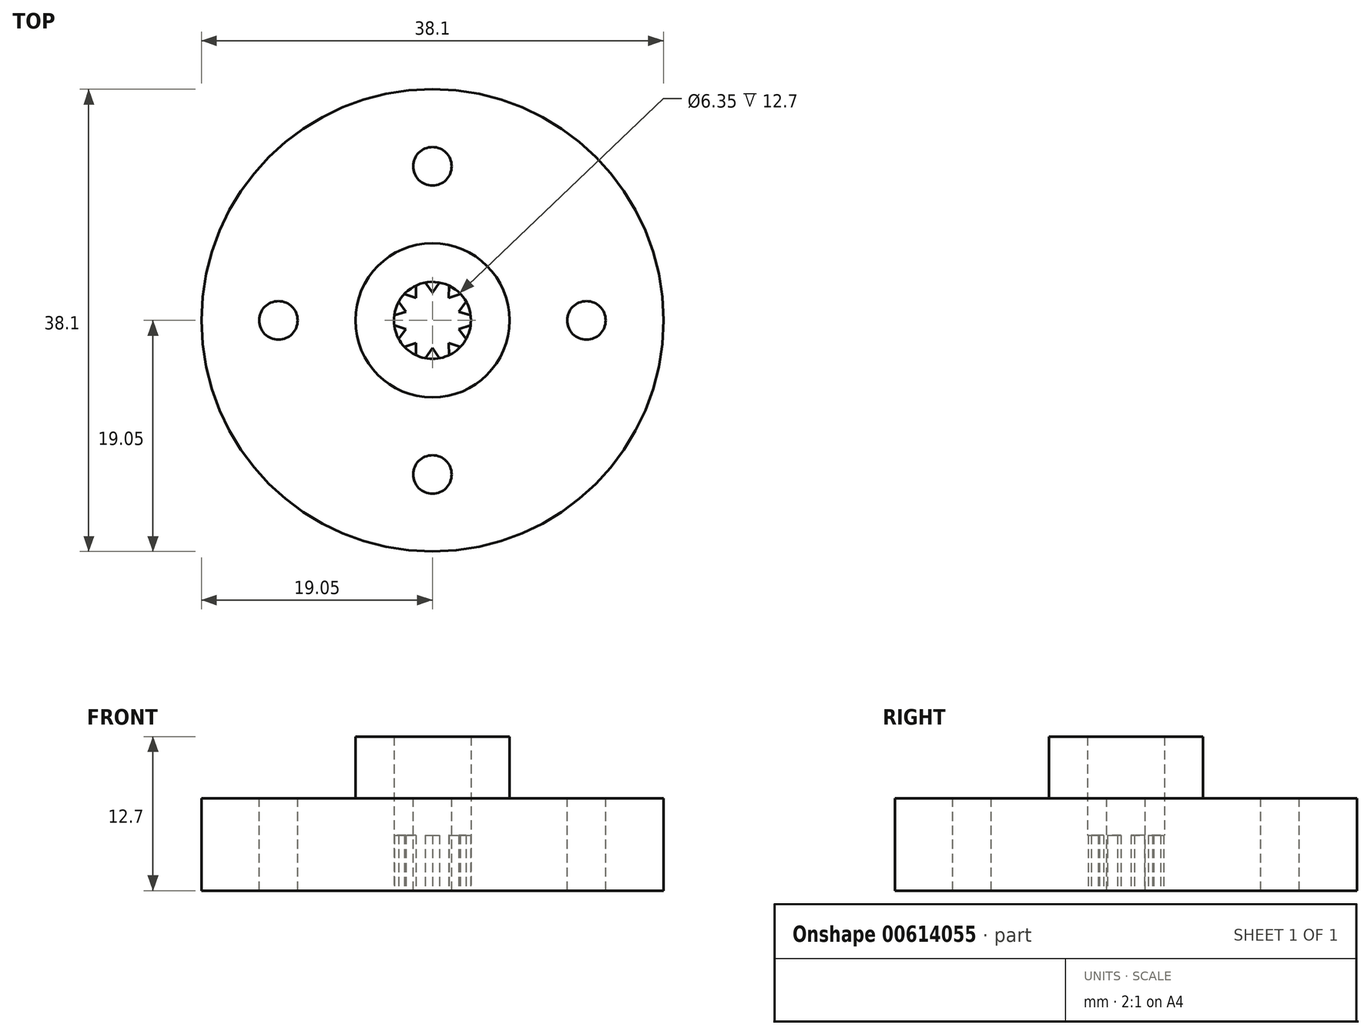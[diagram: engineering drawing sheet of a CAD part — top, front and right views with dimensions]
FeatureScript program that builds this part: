
annotation { "Feature Type Name" : "Feature", "Feature Type Description" : "" }
export const myFeature = defineFeature(function(context is Context, id is Id, definition is map)
    precondition{}
    {
        {
            var Q0;
            Q0=qCreatedBy(makeId("Top.planeOp"),FACE);
            var sketch = newSketch(context, id + "F0", { "sketchPlane" : qUnion([Q0])});
            skCircle(sketch, "E0", {"center": v(0, 0) * mm, "radius": 3.18 * mm});
            skCircle(sketch, "E1", {"center": v(0, 0) * mm, "radius": 6.35 * mm});
            skSolve(sketch);
        }
        {
            var Q0;
            Q0 = qSketchRegion(id + "F0", true);
            extrude(context, id + "F1", {"entities" : qUnion([Q0]), "depth" : 12.7 * mm, "offsetDistance" : 25.4 * mm});
        }
        {
            var Q0;
            Q0=qCreatedBy(makeId("Top.planeOp"),FACE);
            var sketch = newSketch(context, id + "F2", { "sketchPlane" : qUnion([Q0])});
            skCircle(sketch, "E2", {"center": v(0, 0) * mm, "radius": 6.35 * mm});
            skCircle(sketch, "E3", {"center": v(0, 0) * mm, "radius": 19.05 * mm});
            skSolve(sketch);
        }
        {
            var Q0;
            Q0 = qSketchRegion(id + "F2", true);
            extrude(context, id + "F3", {"entities" : qUnion([Q0]), "operationType" : NewBodyOperationType.ADD, "depth" : 7.62 * mm, "offsetDistance" : 25.4 * mm});
        }
        {
            var Q0;
            Q0=qCreatedBy(makeId("Top.planeOp"),FACE);
            var sketch = newSketch(context, id + "F4", { "sketchPlane" : qUnion([Q0])});
            skPoint(sketch, "E4.0.midPoint", {"position": v(0, 2.29) * mm});
            skLineSegment(sketch, "E5", {"start": v(0, 2.29) * mm, "end": v(0, 3.43) * mm});
            skLineSegment(sketch, "E6", {"start": v(0, 3.43) * mm, "end": v(-0.8, 3.43) * mm});
            skLineSegment(sketch, "E7", {"start": v(-0.8, 3.43) * mm, "end": v(0, 2.29) * mm});
            skLineSegment(sketch, "E8", {"start": v(0, 2.29) * mm, "end": v(0.8, 3.43) * mm});
            skLineSegment(sketch, "E9", {"start": v(0.8, 3.43) * mm, "end": v(0, 3.43) * mm});
            skLineSegment(sketch, "E10", {"start": v(1.34, 1.85) * mm, "end": v(2.02, 2.77) * mm});
            skLineSegment(sketch, "E11", {"start": v(2.02, 2.77) * mm, "end": v(1.37, 3.25) * mm});
            skLineSegment(sketch, "E12", {"start": v(1.37, 3.25) * mm, "end": v(1.34, 1.85) * mm});
            skLineSegment(sketch, "E13", {"start": v(1.34, 1.85) * mm, "end": v(2.67, 2.3) * mm});
            skLineSegment(sketch, "E14", {"start": v(2.67, 2.3) * mm, "end": v(2.02, 2.77) * mm});
            skLineSegment(sketch, "E15.0", {"start": v(2.02, 2.77) * mm, "end": v(2.67, 2.3) * mm, "construction": true});
            skLineSegment(sketch, "E16", {"start": v(2.17, 0.7) * mm, "end": v(3.26, 1.06) * mm});
            skLineSegment(sketch, "E17", {"start": v(3.26, 1.06) * mm, "end": v(3.01, 1.82) * mm});
            skLineSegment(sketch, "E18", {"start": v(3.01, 1.82) * mm, "end": v(2.17, 0.7) * mm});
            skLineSegment(sketch, "E19", {"start": v(2.17, 0.7) * mm, "end": v(3.5, 0.3) * mm});
            skLineSegment(sketch, "E20", {"start": v(3.5, 0.3) * mm, "end": v(3.26, 1.06) * mm});
            skLineSegment(sketch, "E21.0", {"start": v(3.26, 1.06) * mm, "end": v(3.5, 0.3) * mm, "construction": true});
            skLineSegment(sketch, "E22.MirrorCS", {"start": v(-0.8, -3.43) * mm, "end": v(0, -2.29) * mm});
            skLineSegment(sketch, "E23.MirrorCS", {"start": v(0, -2.29) * mm, "end": v(0, -3.43) * mm});
            skLineSegment(sketch, "E24.MirrorCS", {"start": v(0, -3.43) * mm, "end": v(-0.8, -3.43) * mm});
            skLineSegment(sketch, "E25.MirrorCS", {"start": v(0.8, -3.43) * mm, "end": v(0, -3.43) * mm});
            skLineSegment(sketch, "E26.MirrorCS", {"start": v(0, -2.29) * mm, "end": v(0.8, -3.43) * mm});
            skLineSegment(sketch, "E27.MirrorCS", {"start": v(2.02, -2.77) * mm, "end": v(1.37, -3.25) * mm});
            skLineSegment(sketch, "E28.MirrorCS", {"start": v(1.37, -3.25) * mm, "end": v(1.34, -1.85) * mm});
            skLineSegment(sketch, "E29.MirrorCS", {"start": v(1.34, -1.85) * mm, "end": v(2.02, -2.77) * mm});
            skLineSegment(sketch, "E30.MirrorCS", {"start": v(2.02, -2.77) * mm, "end": v(2.67, -2.3) * mm, "construction": true});
            skLineSegment(sketch, "E31.MirrorCS", {"start": v(1.34, -1.85) * mm, "end": v(2.67, -2.3) * mm});
            skLineSegment(sketch, "E32.MirrorCS", {"start": v(3.26, -1.06) * mm, "end": v(3.01, -1.82) * mm});
            skLineSegment(sketch, "E33.MirrorCS", {"start": v(3.01, -1.82) * mm, "end": v(2.17, -0.7) * mm});
            skLineSegment(sketch, "E34.MirrorCS", {"start": v(2.17, -0.7) * mm, "end": v(3.26, -1.06) * mm});
            skLineSegment(sketch, "E35.MirrorCS", {"start": v(2.17, -0.7) * mm, "end": v(3.5, -0.3) * mm});
            skLineSegment(sketch, "E36.MirrorCS", {"start": v(3.26, -1.06) * mm, "end": v(3.5, -0.3) * mm, "construction": true});
            skLineSegment(sketch, "E37.MirrorCS", {"start": v(-2.02, 2.77) * mm, "end": v(-2.67, 2.3) * mm, "construction": true});
            skLineSegment(sketch, "E38.MirrorCS", {"start": v(-1.34, 1.85) * mm, "end": v(-2.02, 2.77) * mm});
            skLineSegment(sketch, "E39.MirrorCS", {"start": v(-2.02, 2.77) * mm, "end": v(-1.37, 3.25) * mm});
            skLineSegment(sketch, "E40.MirrorCS", {"start": v(-1.37, 3.25) * mm, "end": v(-1.34, 1.85) * mm});
            skLineSegment(sketch, "E41.MirrorCS", {"start": v(-1.34, 1.85) * mm, "end": v(-2.67, 2.3) * mm});
            skLineSegment(sketch, "E42.MirrorCS", {"start": v(-3.26, 1.06) * mm, "end": v(-3.01, 1.82) * mm});
            skLineSegment(sketch, "E43.MirrorCS", {"start": v(-3.01, 1.82) * mm, "end": v(-2.17, 0.7) * mm});
            skLineSegment(sketch, "E44.MirrorCS", {"start": v(-2.17, 0.7) * mm, "end": v(-3.26, 1.06) * mm});
            skLineSegment(sketch, "E45.MirrorCS", {"start": v(-2.17, 0.7) * mm, "end": v(-3.5, 0.3) * mm});
            skLineSegment(sketch, "E46.MirrorCS", {"start": v(-3.26, 1.06) * mm, "end": v(-3.5, 0.3) * mm, "construction": true});
            skLineSegment(sketch, "E47.MirrorCS", {"start": v(-3.26, -1.06) * mm, "end": v(-3.5, -0.3) * mm, "construction": true});
            skLineSegment(sketch, "E48.MirrorCS", {"start": v(-2.17, -0.7) * mm, "end": v(-3.5, -0.3) * mm});
            skLineSegment(sketch, "E49.MirrorCS", {"start": v(-2.17, -0.7) * mm, "end": v(-3.26, -1.06) * mm});
            skLineSegment(sketch, "E50.MirrorCS", {"start": v(-3.26, -1.06) * mm, "end": v(-3.01, -1.82) * mm});
            skLineSegment(sketch, "E51.MirrorCS", {"start": v(-3.01, -1.82) * mm, "end": v(-2.17, -0.7) * mm});
            skLineSegment(sketch, "E52.MirrorCS", {"start": v(-1.34, -1.85) * mm, "end": v(-2.67, -2.3) * mm});
            skLineSegment(sketch, "E53.MirrorCS", {"start": v(-2.02, -2.77) * mm, "end": v(-2.67, -2.3) * mm, "construction": true});
            skLineSegment(sketch, "E54.MirrorCS", {"start": v(-2.02, -2.77) * mm, "end": v(-1.37, -3.25) * mm});
            skLineSegment(sketch, "E55.MirrorCS", {"start": v(-1.37, -3.25) * mm, "end": v(-1.34, -1.85) * mm});
            skLineSegment(sketch, "E56.MirrorCS", {"start": v(-1.34, -1.85) * mm, "end": v(-2.02, -2.77) * mm});
            skLineSegment(sketch, "E57", {"start": v(-3.5, 0.3) * mm, "end": v(-3.26, 1.06) * mm});
            skLineSegment(sketch, "E58", {"start": v(-3.5, -0.3) * mm, "end": v(-3.26, -1.06) * mm});
            skLineSegment(sketch, "E59", {"start": v(-2.67, -2.3) * mm, "end": v(-2.02, -2.77) * mm});
            skLineSegment(sketch, "E60", {"start": v(2.02, -2.77) * mm, "end": v(2.67, -2.3) * mm});
            skLineSegment(sketch, "E61", {"start": v(-2.02, 2.77) * mm, "end": v(-2.67, 2.3) * mm});
            skLineSegment(sketch, "E62", {"start": v(3.5, -0.3) * mm, "end": v(3.26, -1.06) * mm});
            skSolve(sketch);
        }
        {
            var Q0;
            Q0 = qSketchRegion(id + "F4", true);
            extrude(context, id + "F5", {"entities" : qUnion([Q0]), "operationType" : NewBodyOperationType.ADD, "depth" : 4.57 * mm, "offsetDistance" : 25.4 * mm});
        }
        {
            var Q0;
            Q0=makeQuery(id+"F3.opExtrude","CAP_FACE",FACE,{"disambiguationData":[OSD([sQuery(id+"F2.wireOp",EDGE,"E2"),sQuery(id+"F2.wireOp",EDGE,"E3")])],"isStart":false});
            var sketch = newSketch(context, id + "F6", { "sketchPlane" : qUnion([Q0])});
            skPoint(sketch, "E63", {"position": v(12.7, 0) * mm});
            skPoint(sketch, "E64", {"position": v(0, -12.7) * mm});
            skPoint(sketch, "E65", {"position": v(-12.7, 0) * mm});
            skPoint(sketch, "E66", {"position": v(0, 12.7) * mm});
            skSolve(sketch);
        }
        {
            var Q0;
            Q0=sQuery(id+"F6.wireOp",VERTEX,"E64");
            var Q1;
            Q1=sQuery(id+"F6.wireOp",VERTEX,"E65");
            var Q2;
            Q2=sQuery(id+"F6.wireOp",VERTEX,"E66");
            var Q3;
            Q3=sQuery(id+"F6.wireOp",VERTEX,"E63");
            var Q4;
            Q4=makeQuery(id+"F1.opExtrude","SWEPT_BODY",BODY,{"disambiguationData":[OSD([sQuery(id+"F0.wireOp",EDGE,"E0"),sQuery(id+"F0.wireOp",EDGE,"E1")])]});
            hole(context, id + "F7", {"style" : HoleStyle.SIMPLE, "endStyle" : HoleEndStyle.THROUGH, "holeDiameter" : 3.17 * mm, "majorDiameter" : 6.35 * mm, "isTappedThrough" : true, "tappedDepth" : 12.7 * mm, "tapClearance" : 3, "startFromSketch" : true, "locations" : qUnion([Q0, Q1, Q2, Q3]), "scope" : qUnion([Q4])});
        }
    });
